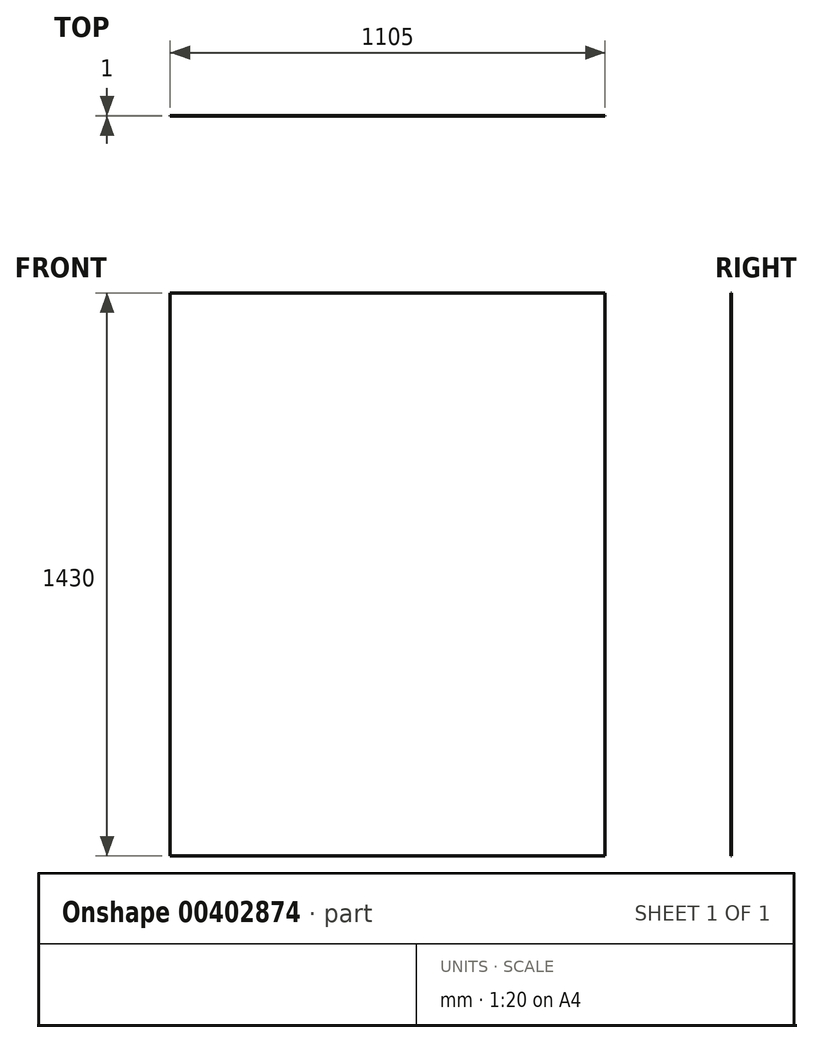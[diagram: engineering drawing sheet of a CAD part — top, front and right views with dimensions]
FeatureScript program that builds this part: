
annotation { "Feature Type Name" : "Feature", "Feature Type Description" : "" }
export const myFeature = defineFeature(function(context is Context, id is Id, definition is map)
    precondition{}
    {
        {
            var Q0;
            Q0=qCreatedBy(makeId("Front.planeOp"),FACE);
            var sketch = newSketch(context, id + "F0", { "sketchPlane" : qUnion([Q0])});
            skLineSegment(sketch, "E0.bottom", {"start": v(-552.5, 715) * mm, "end": v(552.5, 715) * mm});
            skLineSegment(sketch, "E0.top", {"start": v(-552.5, -715) * mm, "end": v(552.5, -715) * mm});
            skLineSegment(sketch, "E0.left", {"start": v(-552.5, 715) * mm, "end": v(-552.5, -715) * mm});
            skLineSegment(sketch, "E0.right", {"start": v(552.5, 715) * mm, "end": v(552.5, -715) * mm});
            skPoint(sketch, "E0.middle", {"position": v(0, 0) * mm});
            skSolve(sketch);
        }
        {
            var Q0;
            Q0=makeQuery(id+"F0.imprint","IMPRINT",FACE,{"disambiguationData":[TD([[makeQuery(id+"F0.imprint","IMPRINT",EDGE,{"derivedFrom":sQuery(id+"F0.wireOp",EDGE,"E0.bottom")}),-1.0]])]});
            extrude(context, id + "F1", {"entities" : qUnion([Q0]), "depth" : 1 * mm});
        }
    });
